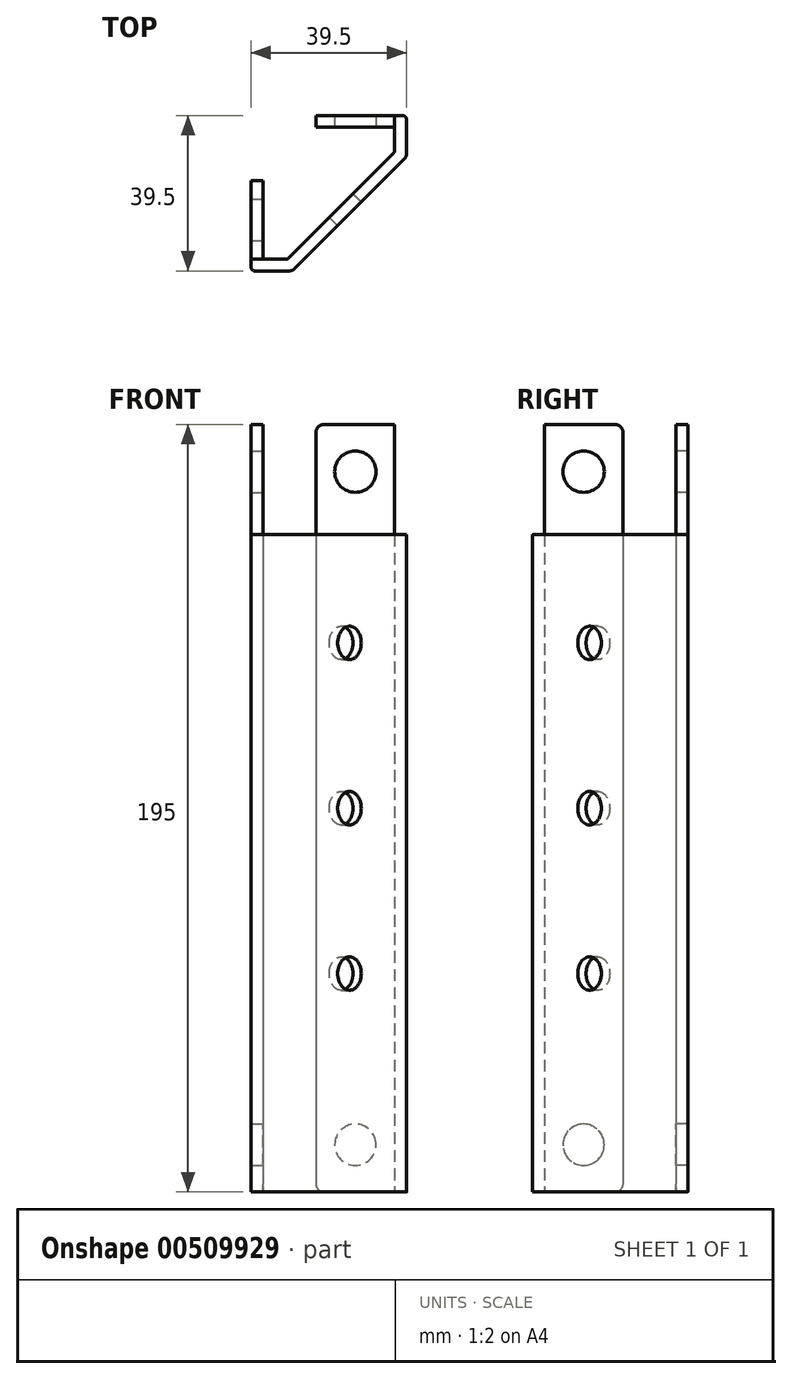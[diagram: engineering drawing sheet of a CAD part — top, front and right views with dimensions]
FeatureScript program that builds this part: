
annotation { "Feature Type Name" : "Feature", "Feature Type Description" : "" }
export const myFeature = defineFeature(function(context is Context, id is Id, definition is map)
    precondition{}
    {
        {
            var Q0;
            Q0=qCreatedBy(makeId("Top.planeOp"),FACE);
            var sketch = newSketch(context, id + "F0", { "sketchPlane" : qUnion([Q0])});
            skLineSegment(sketch, "E0", {"start": v(0, 53.87) * mm, "end": v(0, -58.58) * mm, "construction": true});
            skLineSegment(sketch, "E1", {"start": v(-55.23, 0) * mm, "end": v(53.75, 0) * mm, "construction": true});
            skLineSegment(sketch, "E2.bottom", {"start": v(-19.75, 19.75) * mm, "end": v(19.75, 19.75) * mm, "construction": true});
            skLineSegment(sketch, "E2.top", {"start": v(-19.75, -19.75) * mm, "end": v(19.75, -19.75) * mm, "construction": true});
            skLineSegment(sketch, "E2.left", {"start": v(-19.75, 19.75) * mm, "end": v(-19.75, -19.75) * mm, "construction": true});
            skLineSegment(sketch, "E2.right", {"start": v(19.75, 19.75) * mm, "end": v(19.75, -19.75) * mm, "construction": true});
            skLineSegment(sketch, "E3", {"start": v(-19.75, -19.75) * mm, "end": v(-19.75, 3.25) * mm});
            skLineSegment(sketch, "E4", {"start": v(-19.75, 3.25) * mm, "end": v(-16.75, 3.25) * mm});
            skLineSegment(sketch, "E5", {"start": v(-16.75, 3.25) * mm, "end": v(-16.75, -16.75) * mm});
            skLineSegment(sketch, "E6", {"start": v(-19.75, -19.75) * mm, "end": v(-9.25, -19.75) * mm});
            skLineSegment(sketch, "E7", {"start": v(-9.25, -19.75) * mm, "end": v(19.75, 9.25) * mm, "construction": true});
            skLineSegment(sketch, "E8", {"start": v(-16.75, -6.75) * mm, "end": v(-8.75, -6.75) * mm, "construction": true});
            skLineSegment(sketch, "E9", {"start": v(-8.75, -6.75) * mm, "end": v(-8.75, -15.25) * mm, "construction": true});
            skLineSegment(sketch, "E10.0", {"start": v(-10.5, -16.75) * mm, "end": v(16.75, 10.5) * mm});
            skLineSegment(sketch, "E11", {"start": v(-16.75, -16.75) * mm, "end": v(-10.5, -16.75) * mm});
            skLineSegment(sketch, "E12.0", {"start": v(-10.66, -18.34) * mm, "end": v(18.84, 11.16) * mm, "construction": true});
            skLineSegment(sketch, "E13", {"start": v(-9.25, -19.75) * mm, "end": v(19.75, 9.25) * mm});
            skLineSegment(sketch, "E14", {"start": v(19.75, 9.25) * mm, "end": v(19.75, 19.75) * mm});
            skLineSegment(sketch, "E15", {"start": v(19.75, 19.75) * mm, "end": v(-3.25, 19.75) * mm});
            skLineSegment(sketch, "E16", {"start": v(-3.25, 19.75) * mm, "end": v(-3.25, 16.75) * mm});
            skLineSegment(sketch, "E17", {"start": v(-3.25, 16.75) * mm, "end": v(16.75, 16.75) * mm});
            skLineSegment(sketch, "E18", {"start": v(16.75, 16.75) * mm, "end": v(16.75, 10.5) * mm});
            skSolve(sketch);
        }
        {
            var Q0;
            Q0 = qSketchRegion(id + "F0", true);
            extrude(context, id + "F1", {"entities" : qUnion([Q0]), "depth" : 195 * mm, "symmetric" : true});
        }
        {
            var Q0;
            Q0=makeQuery(id+"F1.opExtrude","CAP_FACE",FACE,{"disambiguationData":[OSD([sQuery(id+"F0.wireOp",EDGE,"E3"),sQuery(id+"F0.wireOp",EDGE,"E4"),sQuery(id+"F0.wireOp",EDGE,"E5"),sQuery(id+"F0.wireOp",EDGE,"E6"),sQuery(id+"F0.wireOp",EDGE,"E10.0"),sQuery(id+"F0.wireOp",EDGE,"E11"),sQuery(id+"F0.wireOp",EDGE,"E13"),sQuery(id+"F0.wireOp",EDGE,"E14"),sQuery(id+"F0.wireOp",EDGE,"E15"),sQuery(id+"F0.wireOp",EDGE,"E16"),sQuery(id+"F0.wireOp",EDGE,"E17"),sQuery(id+"F0.wireOp",EDGE,"E18")])],"isStart":false});
            var sketch = newSketch(context, id + "F2", { "sketchPlane" : qUnion([Q0])});
            skLineSegment(sketch, "E19.0", {"start": v(-16.75, -16.75) * mm, "end": v(-10.5, -16.75) * mm});
            skLineSegment(sketch, "E19.1", {"start": v(-10.5, -16.75) * mm, "end": v(16.75, 10.5) * mm});
            skLineSegment(sketch, "E19.2", {"start": v(16.75, 16.75) * mm, "end": v(16.75, 10.5) * mm});
            skLineSegment(sketch, "E19.3", {"start": v(19.75, 9.25) * mm, "end": v(19.75, 19.75) * mm});
            skLineSegment(sketch, "E19.4", {"start": v(-9.25, -19.75) * mm, "end": v(19.75, 9.25) * mm});
            skLineSegment(sketch, "E19.5", {"start": v(-19.75, -19.75) * mm, "end": v(-9.25, -19.75) * mm});
            skLineSegment(sketch, "E20", {"start": v(-16.75, -16.75) * mm, "end": v(-19.75, -16.75) * mm});
            skLineSegment(sketch, "E21", {"start": v(-19.75, -16.75) * mm, "end": v(-19.75, -19.75) * mm});
            skLineSegment(sketch, "E22", {"start": v(16.75, 16.75) * mm, "end": v(16.75, 19.75) * mm});
            skLineSegment(sketch, "E23", {"start": v(16.75, 19.75) * mm, "end": v(19.75, 19.75) * mm});
            skSolve(sketch);
        }
        {
            var Q0;
            Q0 = qSketchRegion(id + "F2", true);
            extrude(context, id + "F3", {"entities" : qUnion([Q0]), "operationType" : NewBodyOperationType.REMOVE, "oppositeDirection" : true, "depth" : 28 * mm});
        }
        {
            var Q0;
            Q0=makeQuery(id+"F1.opExtrude","SWEPT_FACE",FACE,{"disambiguationData":[OSD([sQuery(id+"F0.wireOp",EDGE,"E13")])]});
            var sketch = newSketch(context, id + "F4", { "sketchPlane" : qUnion([Q0])});
            skLineSegment(sketch, "E24", {"start": v(0, 69.5) * mm, "end": v(0, -69.5) * mm, "construction": true});
            skLineSegment(sketch, "E25", {"start": v(-20.5, 0) * mm, "end": v(20.5, 0) * mm, "construction": true});
            skCircle(sketch, "E26", {"center": v(0, 42) * mm, "radius": 4.25 * mm});
            skCircle(sketch, "E27.MirrorC", {"center": v(0, -42) * mm, "radius": 4.25 * mm});
            skCircle(sketch, "E28", {"center": v(0, 0) * mm, "radius": 4.25 * mm});
            skSolve(sketch);
        }
        {
            var Q0;
            Q0 = qSketchRegion(id + "F4", true);
            extrude(context, id + "F5", {"entities" : qUnion([Q0]), "operationType" : NewBodyOperationType.REMOVE, "oppositeDirection" : true, "depth" : 25 * mm});
        }
        {
            var Q0;
            Q0=makeQuery(id+"F1.opExtrude","SWEPT_FACE",FACE,{"disambiguationData":[OSD([sQuery(id+"F0.wireOp",EDGE,"E5")])]});
            var sketch = newSketch(context, id + "F6", { "sketchPlane" : qUnion([Q0])});
            skLineSegment(sketch, "E29", {"start": v(-6.75, 97.5) * mm, "end": v(-6.75, -97.5) * mm, "construction": true});
            skCircle(sketch, "E30", {"center": v(-6.75, 85.5) * mm, "radius": 5.25 * mm});
            skCircle(sketch, "E31", {"center": v(-6.75, -85.5) * mm, "radius": 5.25 * mm});
            skSolve(sketch);
        }
        {
            var Q0;
            Q0 = qSketchRegion(id + "F6", true);
            extrude(context, id + "F7", {"entities" : qUnion([Q0]), "operationType" : NewBodyOperationType.REMOVE, "oppositeDirection" : true, "depth" : 25 * mm});
        }
        {
            var Q0;
            Q0=makeQuery(id+"F1.opExtrude","SWEPT_FACE",FACE,{"disambiguationData":[OSD([sQuery(id+"F0.wireOp",EDGE,"E17")])]});
            var sketch = newSketch(context, id + "F8", { "sketchPlane" : qUnion([Q0])});
            skLineSegment(sketch, "E32", {"start": v(6.75, 97.5) * mm, "end": v(6.75, -97.5) * mm, "construction": true});
            skCircle(sketch, "E33", {"center": v(6.75, 85.5) * mm, "radius": 5.25 * mm});
            skCircle(sketch, "E34", {"center": v(6.75, -85.5) * mm, "radius": 5.25 * mm});
            skSolve(sketch);
        }
        {
            var Q0;
            Q0 = qSketchRegion(id + "F8", true);
            extrude(context, id + "F9", {"entities" : qUnion([Q0]), "operationType" : NewBodyOperationType.REMOVE, "oppositeDirection" : true, "depth" : 25 * mm});
        }
        {
            var Q0;
            Q0=makeQuery(id+"F1.opExtrude","SWEPT_EDGE",EDGE,{"disambiguationData":[OSD([sQuery(id+"F0.wireOp",EDGE,"E6"),sQuery(id+"F0.wireOp",EDGE,"E13")])]});
            var Q1;
            Q1=makeQuery(id+"F1.opExtrude","SWEPT_EDGE",EDGE,{"disambiguationData":[OSD([sQuery(id+"F0.wireOp",EDGE,"E13"),sQuery(id+"F0.wireOp",EDGE,"E14")])]});
            var Q2;
            Q2=makeQuery(id+"F3.boolean.opBoolean","COPY",EDGE,{"derivedFrom":makeQuery(id+"F3.opExtrude","CAP_EDGE",EDGE,{"disambiguationData":[OSD([sQuery(id+"F2.wireOp",EDGE,"E19.0"),sQuery(id+"F2.wireOp",EDGE,"E20")])],"isStart":true})});
            var Q3;
            Q3=makeQuery(id+"F1.opExtrude","CAP_EDGE",EDGE,{"disambiguationData":[OSD([sQuery(id+"F0.wireOp",EDGE,"E4")])],"isStart":false});
            var Q4;
            Q4=makeQuery(id+"F1.opExtrude","CAP_EDGE",EDGE,{"disambiguationData":[OSD([sQuery(id+"F0.wireOp",EDGE,"E16")])],"isStart":false});
            var Q5;
            Q5=makeQuery(id+"F3.boolean.opBoolean","COPY",EDGE,{"derivedFrom":makeQuery(id+"F3.opExtrude","CAP_EDGE",EDGE,{"disambiguationData":[OSD([sQuery(id+"F2.wireOp",EDGE,"E19.2"),sQuery(id+"F2.wireOp",EDGE,"E22")])],"isStart":true})});
            var Q6;
            Q6=makeQuery(id+"Fec6EYU1eJzkxKK_1.1.F3.boolean.opBoolean","COPY",EDGE,{"derivedFrom":makeQuery(id+"Fec6EYU1eJzkxKK_1.1.F3.opExtrude","CAP_EDGE",EDGE,{"disambiguationData":[OSD([sQuery(id+"F2.wireOp",EDGE,"E19.0"),sQuery(id+"F2.wireOp",EDGE,"E20")])],"isStart":true})});
            var Q7;
            Q7=makeQuery(id+"F1.opExtrude","CAP_EDGE",EDGE,{"disambiguationData":[OSD([sQuery(id+"F0.wireOp",EDGE,"E4")])],"isStart":true});
            var Q8;
            Q8=makeQuery(id+"F1.opExtrude","CAP_EDGE",EDGE,{"disambiguationData":[OSD([sQuery(id+"F0.wireOp",EDGE,"E16")])],"isStart":true});
            var Q9;
            Q9=makeQuery(id+"Fec6EYU1eJzkxKK_1.1.F3.boolean.opBoolean","COPY",EDGE,{"derivedFrom":makeQuery(id+"Fec6EYU1eJzkxKK_1.1.F3.opExtrude","CAP_EDGE",EDGE,{"disambiguationData":[OSD([sQuery(id+"F2.wireOp",EDGE,"E19.2"),sQuery(id+"F2.wireOp",EDGE,"E22")])],"isStart":true})});
            fillet(context, id + "F10", {"entities" : qUnion([Q0, Q1, Q2, Q3, Q4, Q5, Q6, Q7, Q8, Q9]), "radius" : 2 * mm, "tangentPropagation" : true, "allowEdgeOverflow" : false});
        }
        {
            var Q0;
            Q0=makeQuery(id+"F1.opExtrude","SWEPT_EDGE",EDGE,{"disambiguationData":[OSD([sQuery(id+"F0.wireOp",EDGE,"E10.0"),sQuery(id+"F0.wireOp",EDGE,"E18")])]});
            var Q1;
            Q1=makeQuery(id+"F1.opExtrude","SWEPT_EDGE",EDGE,{"disambiguationData":[OSD([sQuery(id+"F0.wireOp",EDGE,"E10.0"),sQuery(id+"F0.wireOp",EDGE,"E11")])]});
            fillet(context, id + "F11", {"entities" : qUnion([Q0, Q1]), "radius" : 0.5 * mm, "tangentPropagation" : true, "allowEdgeOverflow" : false});
        }
        {
            var Q0;
            Q0=makeQuery(id+"F1.opExtrude","SWEPT_EDGE",EDGE,{"disambiguationData":[OSD([sQuery(id+"F0.wireOp",EDGE,"E3"),sQuery(id+"F0.wireOp",EDGE,"E6")])]});
            var Q1;
            Q1=makeQuery(id+"F1.opExtrude","SWEPT_EDGE",EDGE,{"disambiguationData":[OSD([sQuery(id+"F0.wireOp",EDGE,"E14"),sQuery(id+"F0.wireOp",EDGE,"E15")])]});
            fillet(context, id + "F12", {"entities" : qUnion([Q0, Q1]), "radius" : 1 * mm, "tangentPropagation" : true, "allowEdgeOverflow" : false});
        }
    });
